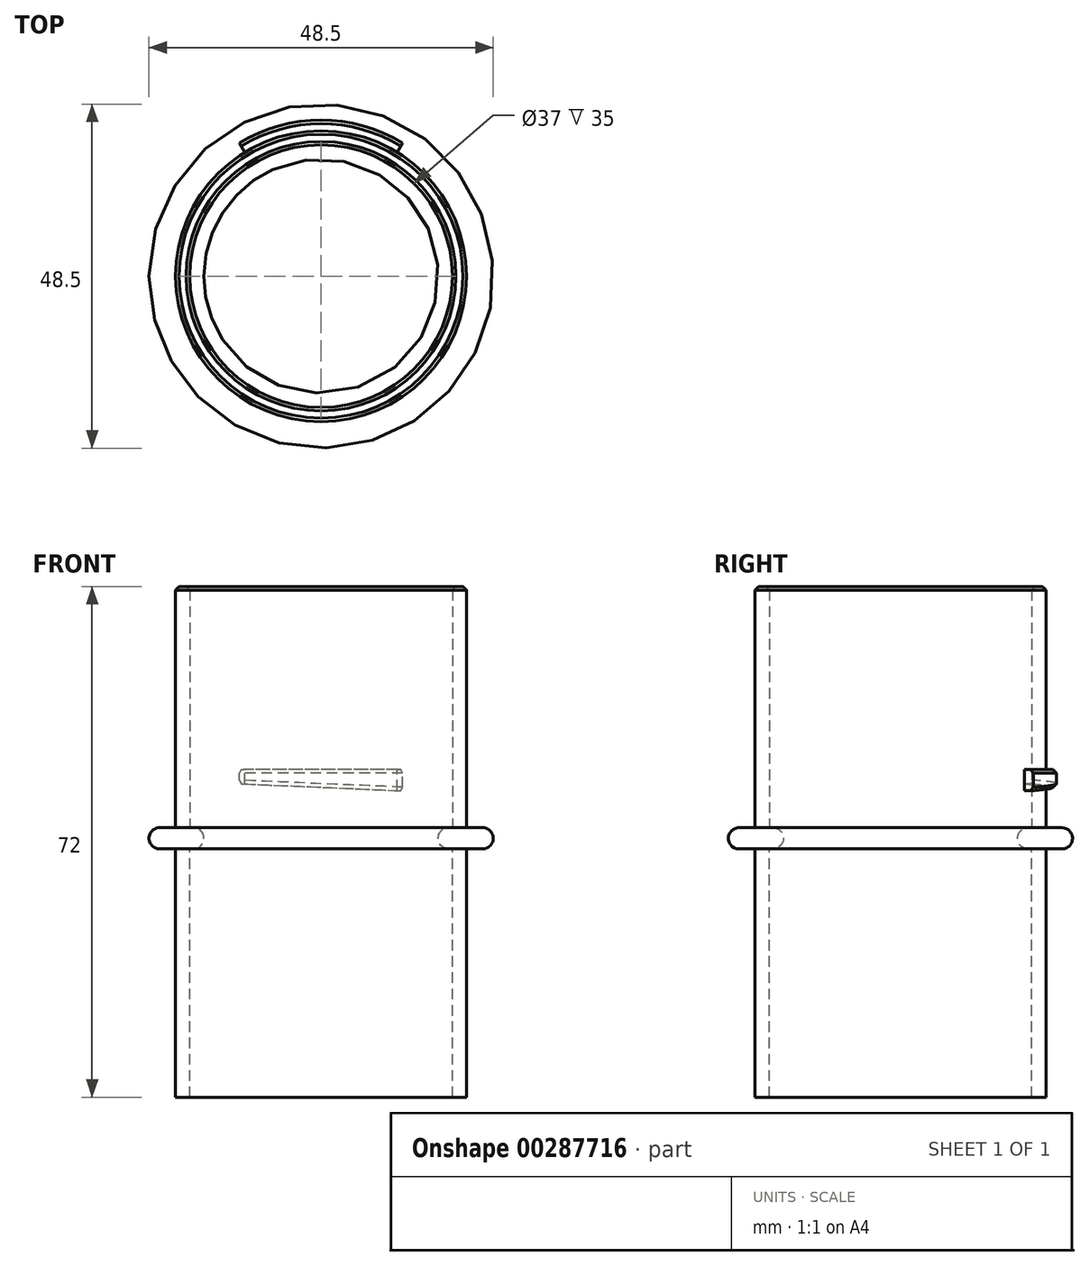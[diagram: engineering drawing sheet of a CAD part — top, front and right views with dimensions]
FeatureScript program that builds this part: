
annotation { "Feature Type Name" : "Feature", "Feature Type Description" : "" }
export const myFeature = defineFeature(function(context is Context, id is Id, definition is map)
    precondition{}
    {
        {
            var Q0;
            Q0=qCreatedBy(makeId("Top.planeOp"),FACE);
            var sketch = newSketch(context, id + "F0", { "sketchPlane" : qUnion([Q0])});
            skCircle(sketch, "E0", {"center": v(0, 0) * mm, "radius": 20.5 * mm});
            skCircle(sketch, "E1", {"center": v(0, 0) * mm, "radius": 18.5 * mm});
            skSolve(sketch);
        }
        {
            var Q0;
            Q0=makeQuery(id+"F0.imprint","IMPRINT",FACE,{"disambiguationData":[TD([[makeQuery(id+"F0.imprint","IMPRINT",EDGE,{"derivedFrom":sQuery(id+"F0.wireOp",EDGE,"E0")}),1.0]])]});
            extrude(context, id + "F1", {"entities" : qUnion([Q0]), "depth" : 34 * mm});
        }
        {
            var Q0;
            Q0=makeQuery(id+"F1.opExtrude","CAP_FACE",FACE,{"disambiguationData":[OSD([sQuery(id+"F0.wireOp",EDGE,"E0"),sQuery(id+"F0.wireOp",EDGE,"E1")])],"isStart":false});
            cPlane(context, id + "F2", {"entities" : qUnion([Q0]), "cplaneType" : CPlaneType.OFFSET, "offset" : 25.8 * mm, "oppositeDirection" : true, "width" : 150 * mm, "height" : 150 * mm});
        }
        {
            var Q0;
            Q0=qCreatedBy(id+"F2.planeOp",FACE);
            var sketch = newSketch(context, id + "F3", { "sketchPlane" : qUnion([Q0])});
            skCircle(sketch, "E2.0", {"center": v(0, 0) * mm, "radius": 20.5 * mm});
            skCircle(sketch, "E3", {"center": v(0, 0) * mm, "radius": 22 * mm});
            skLineSegment(sketch, "E4", {"start": v(-11.5, 18.75) * mm, "end": v(11.5, -18.75) * mm});
            skLineSegment(sketch, "E5", {"start": v(-11.5, -18.75) * mm, "end": v(11.5, 18.75) * mm});
            skLineSegment(sketch, "E6", {"start": v(-11.5, 18.75) * mm, "end": v(0, 20.83) * mm, "construction": true});
            skLineSegment(sketch, "E7", {"start": v(0, 20.83) * mm, "end": v(11.5, 18.75) * mm, "construction": true});
            skSolve(sketch);
        }
        {
            var Q0;
            {var subQ0=sQuery(id+"F3.wireOp",EDGE,"E4");var subQ1=sQuery(id+"F3.wireOp",EDGE,"E2.0");var subQ2=makeQuery(id+"F3.imprint","INTERSECT",VERTEX,{"disambiguationData":[OD(0.0)],"derivedFrom":[subQ1,subQ0]});Q0=makeQuery(id+"F3.imprint","IMPRINT",FACE,{"disambiguationData":[TD([[makeQuery(id+"F3.imprint","IMPRINT",EDGE,{"disambiguationData":[TD([[subQ2,1.0]])],"derivedFrom":subQ1}),-1.0]])]});}
            var Q1;
            {var subQ0=sQuery(id+"F3.wireOp",EDGE,"E5");var subQ1=sQuery(id+"F3.wireOp",EDGE,"E2.0");var subQ2=makeQuery(id+"F3.imprint","INTERSECT",VERTEX,{"disambiguationData":[OD(1.0)],"derivedFrom":[subQ1,subQ0]});Q1=makeQuery(id+"F3.imprint","IMPRINT",FACE,{"disambiguationData":[TD([[makeQuery(id+"F3.imprint","IMPRINT",EDGE,{"disambiguationData":[TD([[subQ2,-1.0]])],"derivedFrom":subQ1}),-1.0]])]});}
            extrude(context, id + "F4", {"entities" : qUnion([Q0, Q1]), "operationType" : NewBodyOperationType.ADD, "oppositeDirection" : true, "depth" : 3 * mm});
        }
        {
            var Q0;
            Q0=qCreatedBy(makeId("Front.planeOp"),FACE);
            cPlane(context, id + "F5", {"entities" : qUnion([Q0]), "cplaneType" : CPlaneType.OFFSET, "offset" : 25 * mm, "width" : 150 * mm, "height" : 150 * mm});
        }
        {
            var Q0;
            Q0=qCreatedBy(id+"F5.planeOp",FACE);
            var sketch = newSketch(context, id + "F6", { "sketchPlane" : qUnion([Q0])});
            skLineSegment(sketch, "E8.0.0", {"start": v(11.5, 8.2) * mm, "end": v(-11.5, 8.2) * mm});
            skLineSegment(sketch, "E8.0.1", {"start": v(-11.5, 8.2) * mm, "end": v(-11.5, 5.2) * mm});
            skLineSegment(sketch, "E8.0.2", {"start": v(-11.5, 5.2) * mm, "end": v(11.5, 5.2) * mm});
            skLineSegment(sketch, "E8.0.3", {"start": v(11.5, 5.2) * mm, "end": v(11.5, 8.2) * mm});
            skLineSegment(sketch, "E9", {"start": v(11.5, 6.2) * mm, "end": v(-11.5, 5.2) * mm});
            skSolve(sketch);
        }
        {
            var Q0;
            {var subQ0=sQuery(id+"F6.wireOp",EDGE,"E8.0.2");Q0=makeQuery(id+"F6.imprint","IMPRINT",FACE,{"disambiguationData":[TD([[makeQuery(id+"F6.imprint","IMPRINT",EDGE,{"derivedFrom":subQ0}),1.0]])]});}
            var Q1;
            Q1=makeQuery(id+"F1.opExtrude","SWEPT_FACE",FACE,{"disambiguationData":[OSD([sQuery(id+"F0.wireOp",EDGE,"E0")])]});
            extrude(context, id + "F7", {"entities" : qUnion([Q0]), "operationType" : NewBodyOperationType.REMOVE, "endBound" : BoundingType.UP_TO_SURFACE, "oppositeDirection" : true, "endBoundEntityFace" : qUnion([Q1]), "depth" : 25 * mm});
        }
        {
            var Q0;
            Q0=qCreatedBy(makeId("Front.planeOp"),FACE);
            cPlane(context, id + "F8", {"entities" : qUnion([Q0]), "cplaneType" : CPlaneType.OFFSET, "offset" : 25 * mm, "oppositeDirection" : true, "width" : 150 * mm, "height" : 150 * mm});
        }
        {
            var Q0;
            Q0=qCreatedBy(id+"F8.planeOp",FACE);
            var sketch = newSketch(context, id + "F9", { "sketchPlane" : qUnion([Q0])});
            skLineSegment(sketch, "E10.0.0", {"start": v(-11.5, 8.2) * mm, "end": v(11.5, 8.2) * mm});
            skLineSegment(sketch, "E10.0.1", {"start": v(11.5, 8.2) * mm, "end": v(11.5, 5.2) * mm});
            skLineSegment(sketch, "E10.0.2", {"start": v(11.5, 5.2) * mm, "end": v(-11.5, 5.2) * mm});
            skLineSegment(sketch, "E10.0.3", {"start": v(-11.5, 5.2) * mm, "end": v(-11.5, 8.2) * mm});
            skLineSegment(sketch, "E11", {"start": v(11.5, 5.2) * mm, "end": v(-11.5, 6.2) * mm});
            skSolve(sketch);
        }
        {
            var Q0;
            {var subQ0=sQuery(id+"F9.wireOp",EDGE,"E10.0.2");Q0=makeQuery(id+"F9.imprint","IMPRINT",FACE,{"disambiguationData":[TD([[makeQuery(id+"F9.imprint","IMPRINT",EDGE,{"derivedFrom":subQ0}),-1.0]])]});}
            var Q1;
            {var subQ0=sQuery(id+"F0.wireOp",EDGE,"E0");Q1=makeQuery(id+"F7.boolean.opBoolean","MERGE",FACE,{"derivedFrom":[makeQuery(id+"F1.opExtrude","SWEPT_FACE",FACE,{"disambiguationData":[OSD([subQ0])]}),makeQuery(id+"F7.opExtrude","CAP_FACE",FACE,{"disambiguationData":[OSD([subQ0])],"isStart":false})]});}
            extrude(context, id + "F10", {"entities" : qUnion([Q0]), "operationType" : NewBodyOperationType.REMOVE, "endBound" : BoundingType.UP_TO_SURFACE, "endBoundEntityFace" : qUnion([Q1]), "depth" : 25 * mm});
        }
        {
            var Q0;
            Q0=makeQuery(id+"F1.opExtrude","CAP_FACE",FACE,{"disambiguationData":[OSD([sQuery(id+"F0.wireOp",EDGE,"E0"),sQuery(id+"F0.wireOp",EDGE,"E1")])],"isStart":true});
            var sketch = newSketch(context, id + "F11", { "sketchPlane" : qUnion([Q0])});
            skCircle(sketch, "E12", {"center": v(0, 0) * mm, "radius": 24.25 * mm});
            skSolve(sketch);
        }
        {
            var Q0;
            Q0=makeQuery(id+"F11.imprint","IMPRINT",FACE,{"disambiguationData":[TD([[makeQuery(id+"F11.imprint","IMPRINT",EDGE,{"derivedFrom":sQuery(id+"F11.wireOp",EDGE,"E12")}),1.0]])]});
            var Q1;
            Q1=makeQuery(id+"F11.imprint","IMPRINT",FACE,{"disambiguationData":[TD([[makeQuery(id+"F11.imprint","IMPRINT",EDGE,{"derivedFrom":makeQuery(id+"F1.opExtrude","CAP_EDGE",EDGE,{"disambiguationData":[OSD([sQuery(id+"F0.wireOp",EDGE,"E0")])],"isStart":true})}),-1.0]])]});
            extrude(context, id + "F12", {"entities" : qUnion([Q0, Q1]), "operationType" : NewBodyOperationType.ADD, "depth" : 3 * mm});
        }
        {
            var Q0;
            Q0=makeQuery(id+"F12.opExtrude","CAP_FACE",FACE,{"disambiguationData":[OSD([sQuery(id+"F0.wireOp",EDGE,"E1"),sQuery(id+"F11.wireOp",EDGE,"E12")])],"isStart":false});
            var sketch = newSketch(context, id + "F13", { "sketchPlane" : qUnion([Q0])});
            skCircle(sketch, "E13.0", {"center": v(0, 0) * mm, "radius": 20.5 * mm});
            skCircle(sketch, "E14", {"center": v(0, 0) * mm, "radius": 16.5 * mm});
            skCircle(sketch, "E15.0", {"center": v(0, 0) * mm, "radius": 18.5 * mm});
            skSolve(sketch);
        }
        {
            var Q0;
            Q0=makeQuery(id+"F13.imprint","IMPRINT",FACE,{"disambiguationData":[TD([[makeQuery(id+"F13.imprint","IMPRINT",EDGE,{"derivedFrom":sQuery(id+"F13.wireOp",EDGE,"E14")}),-1.0]])]});
            extrude(context, id + "F14", {"entities" : qUnion([Q0]), "operationType" : NewBodyOperationType.ADD, "oppositeDirection" : true, "depth" : 3 * mm});
        }
        {
            var Q0;
            Q0=makeQuery(id+"F13.imprint","IMPRINT",FACE,{"disambiguationData":[TD([[makeQuery(id+"F13.imprint","IMPRINT",EDGE,{"derivedFrom":sQuery(id+"F13.wireOp",EDGE,"E13.0")}),1.0]])]});
            extrude(context, id + "F15", {"entities" : qUnion([Q0]), "operationType" : NewBodyOperationType.ADD, "depth" : 35 * mm});
        }
        {
            var Q0;
            Q0=makeQuery(id+"F1.opExtrude","CAP_EDGE",EDGE,{"disambiguationData":[OSD([sQuery(id+"F0.wireOp",EDGE,"E0")])],"isStart":false});
            var Q1;
            Q1=makeQuery(id+"F1.opExtrude","CAP_EDGE",EDGE,{"disambiguationData":[OSD([sQuery(id+"F0.wireOp",EDGE,"E1")])],"isStart":false});
            var Q2;
            {var subQ0=sQuery(id+"F3.wireOp",EDGE,"E3");Q2=makeQuery(id+"F4.opExtrude","CAP_EDGE",EDGE,{"disambiguationData":[OSD([subQ0]),TDD([makeQuery(id+"F3.imprint","IMPRINT",EDGE,{"disambiguationData":[TD([[makeQuery(id+"F3.imprint","INTERSECT",VERTEX,{"disambiguationData":[OD(1.0)],"derivedFrom":[subQ0,sQuery(id+"F3.wireOp",EDGE,"E4")]}),1.0]])],"derivedFrom":subQ0})])],"isStart":true});}
            var Q3;
            {var subQ0=sQuery(id+"F3.wireOp",EDGE,"E3");Q3=makeQuery(id+"F7.boolean.opBoolean","INTERSECT",EDGE,{"derivedFrom":[makeQuery(id+"F4.opExtrude","SWEPT_FACE",FACE,{"disambiguationData":[OSD([subQ0]),TDD([makeQuery(id+"F3.imprint","IMPRINT",EDGE,{"disambiguationData":[TD([[makeQuery(id+"F3.imprint","INTERSECT",VERTEX,{"disambiguationData":[OD(1.0)],"derivedFrom":[subQ0,sQuery(id+"F3.wireOp",EDGE,"E4")]}),1.0]])],"derivedFrom":subQ0})])]}),makeQuery(id+"F7.opExtrude","SWEPT_FACE",FACE,{"disambiguationData":[OSD([sQuery(id+"F6.wireOp",EDGE,"E9")])]})]});}
            var Q4;
            {var subQ0=sQuery(id+"F3.wireOp",EDGE,"E3");Q4=makeQuery(id+"F4.opExtrude","CAP_EDGE",EDGE,{"disambiguationData":[OSD([subQ0]),TDD([makeQuery(id+"F3.imprint","IMPRINT",EDGE,{"disambiguationData":[TD([[makeQuery(id+"F3.imprint","INTERSECT",VERTEX,{"disambiguationData":[OD(0.0)],"derivedFrom":[subQ0,sQuery(id+"F3.wireOp",EDGE,"E4")]}),1.0]])],"derivedFrom":subQ0})])],"isStart":true});}
            var Q5;
            {var subQ0=sQuery(id+"F3.wireOp",EDGE,"E3");Q5=makeQuery(id+"F10.boolean.opBoolean","INTERSECT",EDGE,{"derivedFrom":[makeQuery(id+"F4.opExtrude","SWEPT_FACE",FACE,{"disambiguationData":[OSD([subQ0]),TDD([makeQuery(id+"F3.imprint","IMPRINT",EDGE,{"disambiguationData":[TD([[makeQuery(id+"F3.imprint","INTERSECT",VERTEX,{"disambiguationData":[OD(0.0)],"derivedFrom":[subQ0,sQuery(id+"F3.wireOp",EDGE,"E4")]}),1.0]])],"derivedFrom":subQ0})])]}),makeQuery(id+"F10.opExtrude","SWEPT_FACE",FACE,{"disambiguationData":[OSD([sQuery(id+"F9.wireOp",EDGE,"E11")])]})]});}
            var Q6;
            Q6=makeQuery(id+"F1.opExtrude","CAP_EDGE",EDGE,{"disambiguationData":[OSD([sQuery(id+"F0.wireOp",EDGE,"E0")])],"isStart":true});
            chamfer(context, id + "F16", {"entities" : qUnion([Q0, Q1, Q2, Q3, Q4, Q5, Q6]), "width" : 0.5 * mm, "tangentPropagation" : true});
        }
        {
            var Q0;
            Q0=makeQuery(id+"F14.opExtrude","CAP_EDGE",EDGE,{"disambiguationData":[OSD([sQuery(id+"F13.wireOp",EDGE,"E14")])],"isStart":true});
            var Q1;
            Q1=makeQuery(id+"F14.opExtrude","CAP_EDGE",EDGE,{"disambiguationData":[OSD([sQuery(id+"F13.wireOp",EDGE,"E14")])],"isStart":false});
            var Q2;
            Q2=makeQuery(id+"F15.opExtrude","CAP_EDGE",EDGE,{"disambiguationData":[OSD([sQuery(id+"F13.wireOp",EDGE,"E13.0")])],"isStart":true});
            var Q3;
            Q3=makeQuery(id+"F12.opExtrude","CAP_EDGE",EDGE,{"disambiguationData":[OSD([sQuery(id+"F11.wireOp",EDGE,"E12")])],"isStart":false});
            var Q4;
            Q4=makeQuery(id+"F12.opExtrude","CAP_EDGE",EDGE,{"disambiguationData":[OSD([sQuery(id+"F11.wireOp",EDGE,"E12")])],"isStart":true});
            fillet(context, id + "F17", {"entities" : qUnion([Q0, Q1, Q2, Q3, Q4]), "radius" : 1.5 * mm, "tangentPropagation" : true, "allowEdgeOverflow" : false});
        }
    });
